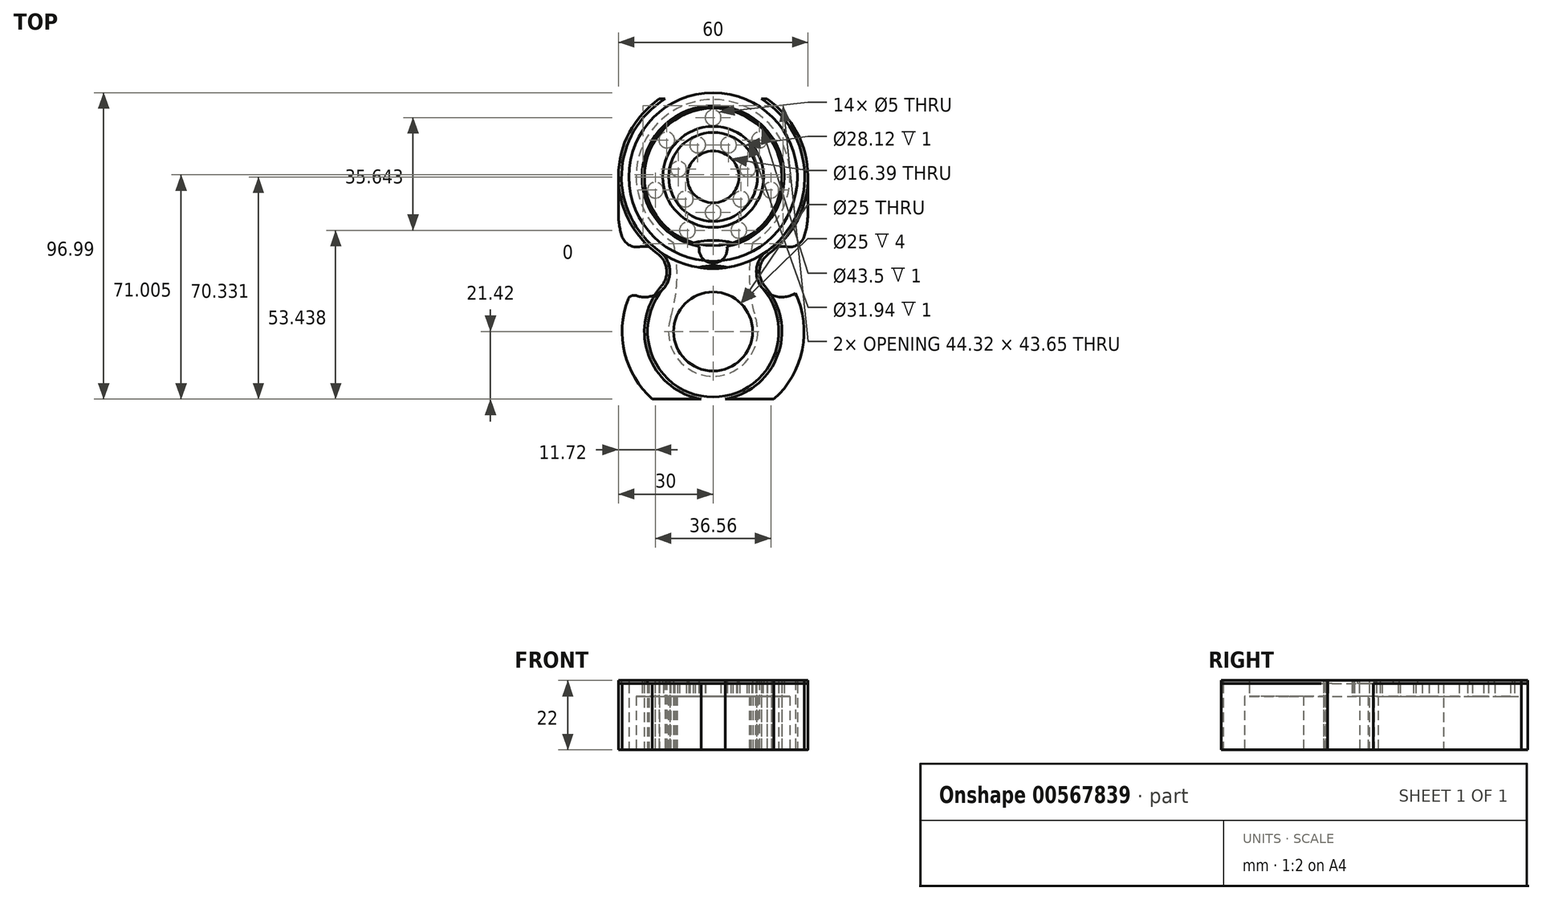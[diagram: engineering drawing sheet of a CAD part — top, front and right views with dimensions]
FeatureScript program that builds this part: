
annotation { "Feature Type Name" : "Feature", "Feature Type Description" : "" }
export const myFeature = defineFeature(function(context is Context, id is Id, definition is map)
    precondition{}
    {
        {
            var Q0;
            Q0=qCreatedBy(makeId("Top.planeOp"),FACE);
            var sketch = newSketch(context, id + "F0", { "sketchPlane" : qUnion([Q0])});
            skLineSegment(sketch, "E0.bottom", {"start": v(-17.07, 47.5) * mm, "end": v(17.07, 47.5) * mm});
            skLineSegment(sketch, "E0.top", {"start": v(-30, -47.5) * mm, "end": v(30, -47.5) * mm});
            skLineSegment(sketch, "E0.left", {"start": v(-30, 22.83) * mm, "end": v(-30, -47.5) * mm});
            skLineSegment(sketch, "E0.right", {"start": v(30, 22.83) * mm, "end": v(30, -47.5) * mm});
            skCircle(sketch, "E1", {"center": v(0, 22.83) * mm, "radius": 22.5 * mm});
            skCircle(sketch, "E2", {"center": v(0, 22.83) * mm, "radius": 15 * mm});
            skCircle(sketch, "E3", {"center": v(0, 41.58) * mm, "radius": 2.5 * mm});
            skCircle(sketch, "E4.1.0", {"center": v(-14.66, 34.52) * mm, "radius": 2.5 * mm});
            skCircle(sketch, "E4.2.0", {"center": v(-18.28, 18.66) * mm, "radius": 2.5 * mm});
            skCircle(sketch, "E4.3.0", {"center": v(-8.14, 5.94) * mm, "radius": 2.5 * mm});
            skCircle(sketch, "E4.4.0", {"center": v(8.14, 5.94) * mm, "radius": 2.5 * mm});
            skCircle(sketch, "E4.5.0", {"center": v(18.28, 18.66) * mm, "radius": 2.5 * mm});
            skCircle(sketch, "E4.6.0", {"center": v(14.66, 34.52) * mm, "radius": 2.5 * mm});
            skCircle(sketch, "E5", {"center": v(-4.88, 32.97) * mm, "radius": 2.5 * mm});
            skCircle(sketch, "E6.1.0", {"center": v(-10.97, 25.33) * mm, "radius": 2.5 * mm});
            skCircle(sketch, "E6.2.0", {"center": v(-8.8, 15.82) * mm, "radius": 2.5 * mm});
            skCircle(sketch, "E6.3.0", {"center": v(0, 11.58) * mm, "radius": 2.5 * mm});
            skCircle(sketch, "E6.4.0", {"center": v(8.8, 15.82) * mm, "radius": 2.5 * mm});
            skCircle(sketch, "E6.5.0", {"center": v(10.97, 25.33) * mm, "radius": 2.5 * mm});
            skCircle(sketch, "E6.6.0", {"center": v(4.88, 32.97) * mm, "radius": 2.5 * mm});
            skArc(sketch, "E7", {"start": v(-17.07, 47.5) * mm, "mid": v(-30, 23.15) * mm, "end": v(-17.6, -1.47) * mm});
            skCircle(sketch, "E8", {"center": v(0, -26.08) * mm, "radius": 12.5 * mm});
            skArc(sketch, "E9", {"start": v(-16.41, -11.79) * mm, "mid": v(-14.73, -6.37) * mm, "end": v(-17.6, -1.47) * mm});
            skArc(sketch, "E10", {"start": v(-16.41, -11.79) * mm, "mid": v(0, -47.84) * mm, "end": v(16.41, -11.79) * mm});
            skArc(sketch, "E11.MirrorCS", {"start": v(17.07, 47.5) * mm, "mid": v(30, 23.15) * mm, "end": v(17.6, -1.47) * mm});
            skArc(sketch, "E12.MirrorCS", {"start": v(16.41, -11.79) * mm, "mid": v(14.73, -6.37) * mm, "end": v(17.6, -1.47) * mm});
            skArc(sketch, "E13", {"start": v(-30, 3.44) * mm, "mid": v(-25.87, -1.8) * mm, "end": v(-20.83, -6.19) * mm});
            skArc(sketch, "E14", {"start": v(19.25, -47.5) * mm, "mid": v(28.74, -24.32) * mm, "end": v(16.49, -2.47) * mm});
            skArc(sketch, "E15.trimOffspring", {"start": v(20.83, -6.19) * mm, "mid": v(25.87, -1.8) * mm, "end": v(30, 3.44) * mm});
            skArc(sketch, "E16.trimOffspring", {"start": v(-16.49, -2.47) * mm, "mid": v(-28.74, -24.32) * mm, "end": v(-19.25, -47.5) * mm});
            skArc(sketch, "E17.trimOffspring", {"start": v(7.67, 1.68) * mm, "mid": v(0, 2.72) * mm, "end": v(-7.67, 1.68) * mm});
            skCircle(sketch, "E18", {"center": v(0, 22.83) * mm, "radius": 29 * mm});
            skCircle(sketch, "E19", {"center": v(-21.72, -7.17) * mm, "radius": 8.04 * mm});
            skCircle(sketch, "E20", {"center": v(21.72, -7.17) * mm, "radius": 8.04 * mm});
            skCircle(sketch, "E21", {"center": v(0, 22.83) * mm, "radius": 26.66 * mm});
            skCircle(sketch, "E22", {"center": v(0, -26.08) * mm, "radius": 20.76 * mm});
            skSolve(sketch);
        }
        {
            var Q0;
            Q0=makeQuery(id+"F0.imprint","IMPRINT",FACE,{"disambiguationData":[TD([[makeQuery(id+"F0.imprint","IMPRINT",EDGE,{"derivedFrom":sQuery(id+"F0.wireOp",EDGE,"E2")}),1.0]])]});
            var Q1;
            Q1=makeQuery(id+"F0.imprint","IMPRINT",FACE,{"disambiguationData":[TD([[makeQuery(id+"F0.imprint","IMPRINT",EDGE,{"derivedFrom":sQuery(id+"F0.wireOp",EDGE,"E2")}),-1.0]])]});
            extrude(context, id + "F1", {"entities" : qUnion([Q0, Q1]), "depth" : 21 * mm, "offsetDistance" : 25 * mm});
        }
        {
            var Q0;
            {var subQ0=sQuery(id+"F0.wireOp",EDGE,"E10");var subQ1=sQuery(id+"F0.wireOp",EDGE,"E0.top");var subQ2=makeQuery(id+"F0.imprint","INTERSECT",VERTEX,{"disambiguationData":[OD(0.0)],"derivedFrom":[subQ1,subQ0]});Q0=makeQuery(id+"F0.imprint","IMPRINT",FACE,{"disambiguationData":[TD([[makeQuery(id+"F0.imprint","IMPRINT",EDGE,{"disambiguationData":[TD([[subQ2,-1.0]])],"derivedFrom":subQ1}),-1.0]])]});}
            var Q1;
            {var subQ0=sQuery(id+"F0.wireOp",EDGE,"E21");var subQ1=sQuery(id+"F0.wireOp",EDGE,"E0.bottom");var subQ2=makeQuery(id+"F0.imprint","INTERSECT",VERTEX,{"disambiguationData":[OD(0.0)],"derivedFrom":[subQ1,subQ0]});Q1=makeQuery(id+"F0.imprint","IMPRINT",FACE,{"disambiguationData":[TD([[makeQuery(id+"F0.imprint","IMPRINT",EDGE,{"disambiguationData":[TD([[subQ2,-1.0]])],"derivedFrom":subQ1}),-1.0]])]});}
            var Q2;
            {var subQ0=sQuery(id+"F0.wireOp",EDGE,"E17.trimOffspring");Q2=makeQuery(id+"F0.imprint","IMPRINT",FACE,{"disambiguationData":[TD([[makeQuery(id+"F0.imprint","IMPRINT",EDGE,{"derivedFrom":subQ0}),1.0]])]});}
            var Q3;
            {var subQ0=sQuery(id+"F0.wireOp",EDGE,"E21");var subQ1=sQuery(id+"F0.wireOp",EDGE,"E0.bottom");var subQ2=makeQuery(id+"F0.imprint","INTERSECT",VERTEX,{"disambiguationData":[OD(0.0)],"derivedFrom":[subQ1,subQ0]});Q3=makeQuery(id+"F0.imprint","IMPRINT",FACE,{"disambiguationData":[TD([[makeQuery(id+"F0.imprint","IMPRINT",EDGE,{"disambiguationData":[TD([[subQ2,-1.0]])],"derivedFrom":subQ1}),1.0]])]});}
            var Q4;
            {var subQ0=sQuery(id+"F0.wireOp",EDGE,"E19");var subQ1=sQuery(id+"F0.wireOp",EDGE,"E18");var subQ2=makeQuery(id+"F0.imprint","INTERSECT",VERTEX,{"derivedFrom":[subQ1,subQ0]});Q4=makeQuery(id+"F0.imprint","IMPRINT",FACE,{"disambiguationData":[TD([[makeQuery(id+"F0.imprint","IMPRINT",EDGE,{"disambiguationData":[TD([[subQ2,-1.0]])],"derivedFrom":subQ1}),-1.0]])]});}
            var Q5;
            {var subQ0=sQuery(id+"F0.wireOp",EDGE,"E22");var subQ1=sQuery(id+"F0.wireOp",EDGE,"E18");var subQ2=makeQuery(id+"F0.imprint","INTERSECT",VERTEX,{"disambiguationData":[OD(1.0)],"derivedFrom":[subQ1,subQ0]});Q5=makeQuery(id+"F0.imprint","IMPRINT",FACE,{"disambiguationData":[TD([[makeQuery(id+"F0.imprint","IMPRINT",EDGE,{"disambiguationData":[TD([[subQ2,-1.0]])],"derivedFrom":subQ1}),-1.0]])]});}
            var Q6;
            Q6=makeQuery(id+"F0.imprint","IMPRINT",FACE,{"disambiguationData":[TD([[makeQuery(id+"F0.imprint","IMPRINT",EDGE,{"derivedFrom":sQuery(id+"F0.wireOp",EDGE,"E8")}),-1.0]])]});
            extrude(context, id + "F2", {"entities" : qUnion([Q0, Q1, Q2, Q3, Q4, Q5, Q6]), "depth" : 21 * mm, "offsetDistance" : 25 * mm});
        }
        {
            var Q0;
            {var subQ0=sQuery(id+"F0.wireOp",EDGE,"E10");var subQ1=sQuery(id+"F0.wireOp",EDGE,"E0.top");var subQ2=makeQuery(id+"F0.imprint","INTERSECT",VERTEX,{"disambiguationData":[OD(0.0)],"derivedFrom":[subQ1,subQ0]});Q0=makeQuery(id+"F0.imprint","IMPRINT",FACE,{"disambiguationData":[TD([[makeQuery(id+"F0.imprint","IMPRINT",EDGE,{"disambiguationData":[TD([[subQ2,-1.0]])],"derivedFrom":subQ1}),-1.0]])]});}
            var Q1;
            {var subQ0=sQuery(id+"F0.wireOp",EDGE,"E16.trimOffspring");var subQ6=sQuery(id+"F0.wireOp",EDGE,"E0.top");var subQ8=makeQuery(id+"F0.imprint","INTERSECT",VERTEX,{"derivedFrom":[subQ6,subQ0]});Q1=makeQuery(id+"F0.imprint","IMPRINT",FACE,{"disambiguationData":[TD([[makeQuery(id+"F0.imprint","IMPRINT",EDGE,{"disambiguationData":[TD([[subQ8,-1.0]])],"derivedFrom":subQ6}),1.0]])]});}
            var Q2;
            {var subQ0=sQuery(id+"F0.wireOp",EDGE,"E14");var subQ1=sQuery(id+"F0.wireOp",EDGE,"E0.top");var subQ2=makeQuery(id+"F0.imprint","INTERSECT",VERTEX,{"derivedFrom":[subQ1,subQ0]});Q2=makeQuery(id+"F0.imprint","IMPRINT",FACE,{"disambiguationData":[TD([[makeQuery(id+"F0.imprint","IMPRINT",EDGE,{"disambiguationData":[TD([[subQ2,1.0]])],"derivedFrom":subQ1}),1.0]])]});}
            var Q3;
            {var subQ0=sQuery(id+"F0.wireOp",EDGE,"E13");Q3=makeQuery(id+"F0.imprint","IMPRINT",FACE,{"disambiguationData":[TD([[makeQuery(id+"F0.imprint","IMPRINT",EDGE,{"derivedFrom":subQ0}),1.0]])]});}
            var Q4;
            {var subQ3=sQuery(id+"F0.wireOp",EDGE,"E15.trimOffspring");Q4=makeQuery(id+"F0.imprint","IMPRINT",FACE,{"disambiguationData":[TD([[makeQuery(id+"F0.imprint","IMPRINT",EDGE,{"derivedFrom":subQ3}),1.0]])]});}
            var Q5;
            {var subQ0=sQuery(id+"F0.wireOp",EDGE,"E18");var subQ4=sQuery(id+"F0.wireOp",EDGE,"E0.bottom");var subQ5=makeQuery(id+"F0.imprint","INTERSECT",VERTEX,{"disambiguationData":[OD(0.0)],"derivedFrom":[subQ4,subQ0]});Q5=makeQuery(id+"F0.imprint","IMPRINT",FACE,{"disambiguationData":[TD([[makeQuery(id+"F0.imprint","IMPRINT",EDGE,{"disambiguationData":[TD([[subQ5,-1.0]])],"derivedFrom":subQ4}),-1.0]])]});}
            var Q6;
            {var subQ0=sQuery(id+"F0.wireOp",EDGE,"E22");var subQ1=sQuery(id+"F0.wireOp",EDGE,"E18");var subQ2=makeQuery(id+"F0.imprint","INTERSECT",VERTEX,{"disambiguationData":[OD(0.0)],"derivedFrom":[subQ1,subQ0]});Q6=makeQuery(id+"F0.imprint","IMPRINT",FACE,{"disambiguationData":[TD([[makeQuery(id+"F0.imprint","IMPRINT",EDGE,{"disambiguationData":[TD([[subQ2,-1.0]])],"derivedFrom":subQ1}),1.0]])]});}
            extrude(context, id + "F3", {"entities" : qUnion([Q0, Q1, Q2, Q3, Q4, Q5, Q6]), "depth" : 21 * mm, "offsetDistance" : 25 * mm});
        }
        {
            var Q0;
            Q0=makeQuery(id+"F3.opExtrude","SWEPT_EDGE",EDGE,{"disambiguationData":[OSD([sQuery(id+"F0.wireOp",EDGE,"E0.left"),sQuery(id+"F0.wireOp",EDGE,"E13")])]});
            var Q1;
            Q1=makeQuery(id+"F3.opExtrude","SWEPT_EDGE",EDGE,{"disambiguationData":[OSD([sQuery(id+"F0.wireOp",EDGE,"E0.right"),sQuery(id+"F0.wireOp",EDGE,"E15.trimOffspring")])]});
            fillet(context, id + "F4", {"entities" : qUnion([Q0, Q1]), "radius" : 25 * mm, "tangentPropagation" : true, "allowEdgeOverflow" : false});
        }
        {
            var Q0;
            {var subQ0=sQuery(id+"F0.wireOp",EDGE,"E10");var subQ1=sQuery(id+"F0.wireOp",EDGE,"E0.top");var subQ2=makeQuery(id+"F0.imprint","INTERSECT",VERTEX,{"disambiguationData":[OD(0.0)],"derivedFrom":[subQ1,subQ0]});Q0=makeQuery(id+"F0.imprint","IMPRINT",FACE,{"disambiguationData":[TD([[makeQuery(id+"F0.imprint","IMPRINT",EDGE,{"disambiguationData":[TD([[subQ2,-1.0]])],"derivedFrom":subQ1}),-1.0]])]});}
            var Q1;
            {var subQ1=sQuery(id+"F0.wireOp",EDGE,"E0.bottom");var subQ5=sQuery(id+"F0.wireOp",EDGE,"E7");var subQ8=makeQuery(id+"F0.imprint","INTERSECT",VERTEX,{"derivedFrom":[subQ1,subQ5]});Q1=makeQuery(id+"F0.imprint","IMPRINT",FACE,{"disambiguationData":[TD([[makeQuery(id+"F0.imprint","IMPRINT",EDGE,{"disambiguationData":[TD([[subQ8,-1.0]])],"derivedFrom":subQ1}),-1.0]])]});}
            var Q2;
            {var subQ1=sQuery(id+"F0.wireOp",EDGE,"E0.bottom");var subQ5=sQuery(id+"F0.wireOp",EDGE,"E11.MirrorCS");var subQ8=makeQuery(id+"F0.imprint","INTERSECT",VERTEX,{"derivedFrom":[subQ1,subQ5]});Q2=makeQuery(id+"F0.imprint","IMPRINT",FACE,{"disambiguationData":[TD([[makeQuery(id+"F0.imprint","IMPRINT",EDGE,{"disambiguationData":[TD([[subQ8,1.0]])],"derivedFrom":subQ1}),-1.0]])]});}
            var Q3;
            {var subQ0=sQuery(id+"F0.wireOp",EDGE,"E10");var subQ1=sQuery(id+"F0.wireOp",EDGE,"E0.top");var subQ5=makeQuery(id+"F0.imprint","INTERSECT",VERTEX,{"disambiguationData":[OD(0.0)],"derivedFrom":[subQ1,subQ0]});Q3=makeQuery(id+"F0.imprint","IMPRINT",FACE,{"disambiguationData":[TD([[makeQuery(id+"F0.imprint","IMPRINT",EDGE,{"disambiguationData":[TD([[subQ5,-1.0]])],"derivedFrom":subQ1}),1.0]])]});}
            var Q4;
            {var subQ1=sQuery(id+"F0.wireOp",EDGE,"E9");var subQ5=sQuery(id+"F0.wireOp",EDGE,"E7");var subQ6=makeQuery(id+"F0.imprint","INTERSECT",VERTEX,{"derivedFrom":[subQ5,subQ1]});Q4=makeQuery(id+"F0.imprint","IMPRINT",FACE,{"disambiguationData":[TD([[makeQuery(id+"F0.imprint","IMPRINT",EDGE,{"disambiguationData":[TD([[subQ6,1.0]])],"derivedFrom":subQ5}),1.0]])]});}
            var Q5;
            {var subQ0=sQuery(id+"F0.wireOp",EDGE,"E12.MirrorCS");var subQ1=sQuery(id+"F0.wireOp",EDGE,"E10");var subQ2=makeQuery(id+"F0.imprint","INTERSECT",VERTEX,{"derivedFrom":[subQ1,subQ0]});Q5=makeQuery(id+"F0.imprint","IMPRINT",FACE,{"disambiguationData":[TD([[makeQuery(id+"F0.imprint","IMPRINT",EDGE,{"disambiguationData":[TD([[subQ2,1.0]])],"derivedFrom":subQ1}),1.0]])]});}
            extrude(context, id + "F5", {"entities" : qUnion([Q0, Q1, Q2, Q3, Q4, Q5]), "depth" : 22 * mm, "offsetDistance" : 25 * mm});
        }
        {
            var Q0;
            Q0=makeQuery(id+"F2.opExtrude","CAP_FACE",FACE,{"disambiguationData":[OSD([sQuery(id+"F0.wireOp",EDGE,"E1"),sQuery(id+"F0.wireOp",EDGE,"E17.trimOffspring"),sQuery(id+"F0.wireOp",EDGE,"E21")])],"isStart":false});
            cPlane(context, id + "F6", {"entities" : qUnion([Q0]), "cplaneType" : CPlaneType.OFFSET, "offset" : 0 * mm, "width" : 150 * mm, "height" : 150 * mm});
        }
        {
            var Q0;
            Q0=qCreatedBy(id+"F6.planeOp",FACE);
            var sketch = newSketch(context, id + "F7", { "sketchPlane" : qUnion([Q0])});
            skCircle(sketch, "E23", {"center": v(0, 0) * mm, "radius": 4.43 * mm});
            skArc(sketch, "E24.0", {"start": v(7.67, 1.68) * mm, "mid": v(0, 45.33) * mm, "end": v(-7.67, 1.68) * mm});
            skCircle(sketch, "E25", {"center": v(0, 22.83) * mm, "radius": 22.5 * mm});
            skCircle(sketch, "E26", {"center": v(0, 22.83) * mm, "radius": 15 * mm});
            skCircle(sketch, "E27", {"center": v(0, 22.83) * mm, "radius": 7.5 * mm});
            skCircle(sketch, "E28", {"center": v(0, 22.83) * mm, "radius": 21.75 * mm});
            skCircle(sketch, "E29", {"center": v(0, 22.83) * mm, "radius": 15.97 * mm});
            skCircle(sketch, "E30", {"center": v(0, 22.83) * mm, "radius": 14.06 * mm});
            skCircle(sketch, "E31", {"center": v(0, 22.83) * mm, "radius": 8.2 * mm});
            skSolve(sketch);
        }
        {
            var Q0;
            Q0=makeQuery(id+"F2.opExtrude","CAP_FACE",FACE,{"disambiguationData":[OSD([sQuery(id+"F0.wireOp",EDGE,"E1"),sQuery(id+"F0.wireOp",EDGE,"E17.trimOffspring"),sQuery(id+"F0.wireOp",EDGE,"E21")])],"isStart":false});
            var Q1;
            Q1=makeQuery(id+"F2.opExtrude","CAP_FACE",FACE,{"disambiguationData":[OSD([sQuery(id+"F0.wireOp",EDGE,"E8"),sQuery(id+"F0.wireOp",EDGE,"E18"),sQuery(id+"F0.wireOp",EDGE,"E19"),sQuery(id+"F0.wireOp",EDGE,"E20"),sQuery(id+"F0.wireOp",EDGE,"E22")])],"isStart":false});
            var Q2;
            Q2=makeQuery(id+"F3.opExtrude","CAP_FACE",FACE,{"disambiguationData":[OSD([sQuery(id+"F0.wireOp",EDGE,"E0.bottom"),sQuery(id+"F0.wireOp",EDGE,"E18"),sQuery(id+"F0.wireOp",EDGE,"E21"),sQuery(id+"F0.wireOp",EDGE,"E22")])],"isStart":false});
            extrude(context, id + "F8", {"entities" : qUnion([Q0, Q1, Q2]), "depth" : 1 * mm, "offsetDistance" : 25 * mm});
        }
        {
            var Q0;
            Q0 = qSketchRegion(id + "F7", true);
            var Q1;
            Q1=makeQuery(id+"F7.imprint","IMPRINT",FACE,{"disambiguationData":[TD([[makeQuery(id+"F7.imprint","IMPRINT",EDGE,{"derivedFrom":sQuery(id+"F7.wireOp",EDGE,"E26")}),1.0]])]});
            var Q2;
            Q2=makeQuery(id+"F7.imprint","IMPRINT",FACE,{"disambiguationData":[TD([[makeQuery(id+"F7.imprint","IMPRINT",EDGE,{"derivedFrom":sQuery(id+"F7.wireOp",EDGE,"E26")}),-1.0]])]});
            var Q3;
            Q3=makeQuery(id+"F7.imprint","IMPRINT",FACE,{"disambiguationData":[TD([[makeQuery(id+"F7.imprint","IMPRINT",EDGE,{"derivedFrom":sQuery(id+"F7.wireOp",EDGE,"E27")}),-1.0]])]});
            var Q4;
            Q4=makeQuery(id+"F7.imprint","IMPRINT",FACE,{"disambiguationData":[TD([[makeQuery(id+"F7.imprint","IMPRINT",EDGE,{"derivedFrom":sQuery(id+"F7.wireOp",EDGE,"E27")}),1.0]])]});
            extrude(context, id + "F9", {"entities" : qUnion([Q0, Q1, Q2, Q3, Q4]), "depth" : 1 * mm, "offsetDistance" : 25 * mm});
        }
        {
            var Q0;
            Q0=makeQuery(id+"F7.imprint","IMPRINT",FACE,{"disambiguationData":[TD([[makeQuery(id+"F7.imprint","IMPRINT",EDGE,{"derivedFrom":sQuery(id+"F7.wireOp",EDGE,"E29")}),-1.0]])]});
            var Q1;
            Q1=makeQuery(id+"F7.imprint","IMPRINT",FACE,{"disambiguationData":[TD([[makeQuery(id+"F7.imprint","IMPRINT",EDGE,{"derivedFrom":sQuery(id+"F7.wireOp",EDGE,"E30")}),1.0]])]});
            var Q2;
            {var subQ0=sQuery(id+"F7.wireOp",EDGE,"E28");var subQ1=sQuery(id+"F7.wireOp",EDGE,"E23");var subQ2=makeQuery(id+"F7.imprint","INTERSECT",VERTEX,{"disambiguationData":[OD(0.0)],"derivedFrom":[subQ1,subQ0]});Q2=makeQuery(id+"F7.imprint","IMPRINT",FACE,{"disambiguationData":[TD([[makeQuery(id+"F7.imprint","IMPRINT",EDGE,{"disambiguationData":[TD([[subQ2,-1.0]])],"derivedFrom":subQ1}),1.0]])]});}
            extrude(context, id + "F10", {"entities" : qUnion([Q0, Q1, Q2]), "depth" : 1 * mm, "offsetDistance" : 25 * mm});
        }
        {
            var Q0;
            {var subQ0=sQuery(id+"F0.wireOp",EDGE,"E19");var subQ1=sQuery(id+"F0.wireOp",EDGE,"E13");Q0=makeQuery(id+"F4.opFillet","BLEND_EDGE",EDGE,{"blendedFrom":[makeQuery(id+"F3.opExtrude","SWEPT_EDGE",EDGE,{"disambiguationData":[OSD([sQuery(id+"F0.wireOp",EDGE,"E0.left"),subQ1])]}),makeQuery(id+"F3.opExtrude","SWEPT_FACE",FACE,{"disambiguationData":[OSD([subQ0]),TDD([makeQuery(id+"F0.imprint","IMPRINT",EDGE,{"disambiguationData":[TD([[makeQuery(id+"F0.imprint","INTERSECT",VERTEX,{"derivedFrom":[sQuery(id+"F0.wireOp",EDGE,"E7"),subQ0]}),-1.0]])],"derivedFrom":subQ0})])]})],"blendedInto":[makeQuery(id+"F3.opExtrude","SWEPT_FACE",FACE,{"disambiguationData":[OSD([subQ0]),TDD([makeQuery(id+"F0.imprint","IMPRINT",EDGE,{"disambiguationData":[TD([[makeQuery(id+"F0.imprint","INTERSECT",VERTEX,{"derivedFrom":[sQuery(id+"F0.wireOp",EDGE,"E7"),subQ0]}),-1.0]])],"derivedFrom":subQ0})])]})]});}
            var Q1;
            {var subQ0=sQuery(id+"F0.wireOp",EDGE,"E20");var subQ1=sQuery(id+"F0.wireOp",EDGE,"E15.trimOffspring");Q1=makeQuery(id+"F4.opFillet","BLEND_EDGE",EDGE,{"blendedFrom":[makeQuery(id+"F3.opExtrude","SWEPT_EDGE",EDGE,{"disambiguationData":[OSD([sQuery(id+"F0.wireOp",EDGE,"E0.right"),subQ1])]}),makeQuery(id+"F3.opExtrude","SWEPT_FACE",FACE,{"disambiguationData":[OSD([subQ0]),TDD([makeQuery(id+"F0.imprint","IMPRINT",EDGE,{"disambiguationData":[TD([[makeQuery(id+"F0.imprint","INTERSECT",VERTEX,{"derivedFrom":[sQuery(id+"F0.wireOp",EDGE,"E11.MirrorCS"),subQ0]}),1.0]])],"derivedFrom":subQ0})])]})],"blendedInto":[makeQuery(id+"F3.opExtrude","SWEPT_FACE",FACE,{"disambiguationData":[OSD([subQ0]),TDD([makeQuery(id+"F0.imprint","IMPRINT",EDGE,{"disambiguationData":[TD([[makeQuery(id+"F0.imprint","INTERSECT",VERTEX,{"derivedFrom":[sQuery(id+"F0.wireOp",EDGE,"E11.MirrorCS"),subQ0]}),1.0]])],"derivedFrom":subQ0})])]})]});}
            fillet(context, id + "F11", {"entities" : qUnion([Q0, Q1]), "radius" : 5 * mm, "tangentPropagation" : true, "allowEdgeOverflow" : false});
        }
        {
            var Q0;
            Q0=makeQuery(id+"F1.opExtrude","CAP_FACE",FACE,{"disambiguationData":[OSD([sQuery(id+"F0.wireOp",EDGE,"E1"),sQuery(id+"F0.wireOp",EDGE,"E3"),sQuery(id+"F0.wireOp",EDGE,"E4.1.0"),sQuery(id+"F0.wireOp",EDGE,"E4.2.0"),sQuery(id+"F0.wireOp",EDGE,"E4.3.0"),sQuery(id+"F0.wireOp",EDGE,"E4.4.0"),sQuery(id+"F0.wireOp",EDGE,"E4.5.0"),sQuery(id+"F0.wireOp",EDGE,"E4.6.0"),sQuery(id+"F0.wireOp",EDGE,"E5"),sQuery(id+"F0.wireOp",EDGE,"E6.1.0"),sQuery(id+"F0.wireOp",EDGE,"E6.2.0"),sQuery(id+"F0.wireOp",EDGE,"E6.3.0"),sQuery(id+"F0.wireOp",EDGE,"E6.4.0"),sQuery(id+"F0.wireOp",EDGE,"E6.5.0"),sQuery(id+"F0.wireOp",EDGE,"E6.6.0"),sQuery(id+"F0.wireOp",EDGE,"E17.trimOffspring")])],"isStart":true});
            cPlane(context, id + "F12", {"entities" : qUnion([Q0]), "cplaneType" : CPlaneType.OFFSET, "offset" : 0 * mm, "width" : 150 * mm, "height" : 150 * mm});
        }
        {
            var Q0;
            Q0=qCreatedBy(id+"F12.planeOp",FACE);
            var sketch = newSketch(context, id + "F13", { "sketchPlane" : qUnion([Q0])});
            skCircle(sketch, "E32", {"center": v(0, -22.97) * mm, "radius": 24.34 * mm});
            skCircle(sketch, "E33", {"center": v(0, 26.08) * mm, "radius": 14.13 * mm});
            skArc(sketch, "E34", {"start": v(13.64, 22.37) * mm, "mid": v(11.48, 10.2) * mm, "end": v(12.56, -2.12) * mm});
            skArc(sketch, "E35.MirrorCS", {"start": v(-13.64, 22.37) * mm, "mid": v(-11.48, 10.2) * mm, "end": v(-12.56, -2.12) * mm});
            skSolve(sketch);
        }
        {
            var Q0;
            Q0 = qSketchRegion(id + "F13", true);
            extrude(context, id + "F14", {"entities" : qUnion([Q0]), "operationType" : NewBodyOperationType.REMOVE, "oppositeDirection" : true, "depth" : 17 * mm, "offsetDistance" : 25 * mm});
        }
        {
            var Q0;
            Q0=makeQuery(id+"F3.opExtrude","SWEPT_EDGE",EDGE,{"disambiguationData":[OSD([sQuery(id+"F0.wireOp",EDGE,"E16.trimOffspring"),sQuery(id+"F0.wireOp",EDGE,"E19")])]});
            var Q1;
            Q1=makeQuery(id+"F3.opExtrude","SWEPT_EDGE",EDGE,{"disambiguationData":[OSD([sQuery(id+"F0.wireOp",EDGE,"E14"),sQuery(id+"F0.wireOp",EDGE,"E20")])]});
            fillet(context, id + "F15", {"entities" : qUnion([Q0, Q1]), "radius" : 2 * mm, "tangentPropagation" : true, "allowEdgeOverflow" : false});
        }
    });
